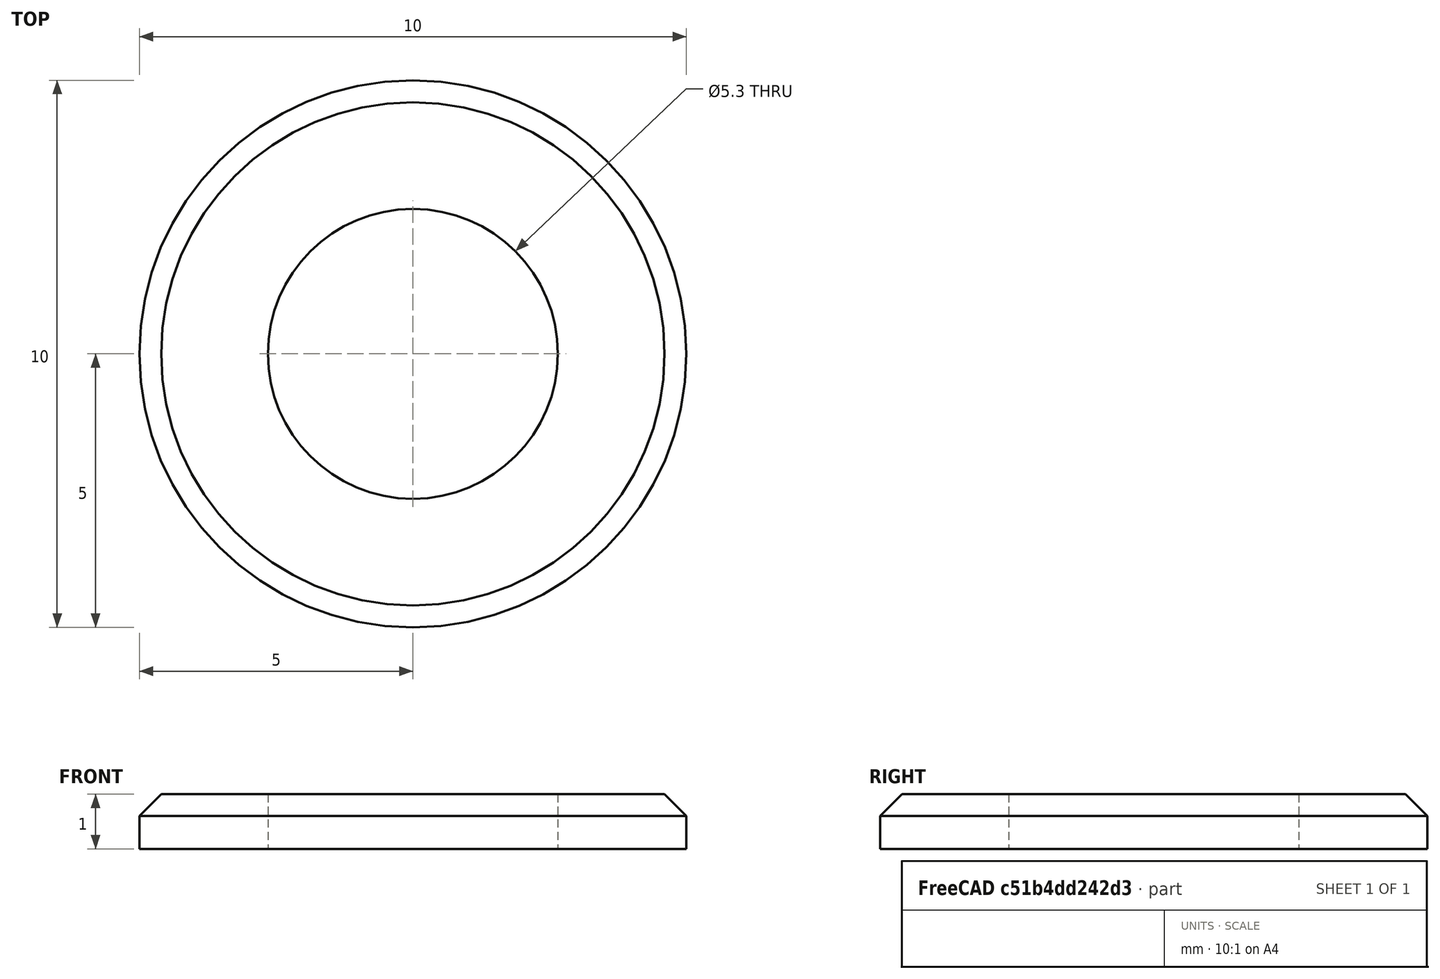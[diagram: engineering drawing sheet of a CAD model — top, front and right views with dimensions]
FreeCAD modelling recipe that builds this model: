
FCSTD DOCUMENT  (FreeCAD 0.15R4651 (Git))
Label: Scheibe_DIN125-B 5,3
License: CC-BY 3.0
LicenseURL: http://creativecommons.org/licenses/by/3.0/
objects: Sketcher::SketchObject×1, PartDesign::Revolution×1
note: 3 computed .brp shape members not serialized (recipe doc carries the construction recipe); baked Part::Feature solids carry a one-line shape summary decoded from their .brp

FEATURE [Sketcher::SketchObject] Sketch
  Placement = pos=(0,0,0) rot=(0.57735,0.57735,0.57735;2.0944rad)
  sketch-geometry (5):
    g0: LineSegment StartX=2.65 StartY=0 StartZ=0 EndX=5 EndY=0 EndZ=0
    g1: LineSegment StartX=5 StartY=0 StartZ=0 EndX=5 EndY=0.6 EndZ=0
    g2: LineSegment StartX=4.6 StartY=1 StartZ=0 EndX=2.65 EndY=1 EndZ=0
    g3: LineSegment StartX=2.65 StartY=1 StartZ=0 EndX=2.65 EndY=0 EndZ=0
    g4: LineSegment StartX=4.6 StartY=1 StartZ=0 EndX=5 EndY=0.6 EndZ=0
  constraints (15):
    c: Coincident(g0,g1)
    c: Coincident(g2,g3)
    c: Coincident(g3,g0)
    c: Horizontal(g0)
    c: Horizontal(g2)
    c: Vertical(g1)
    c: Vertical(g3)
    c: PointOnObject(g0,g-1)
    c: DistanceX(g-1,g2) = 2.65
    c: Coincident(g1,g4)
    c: Coincident(g2,g4)
    c: DistanceY(g3) = -1
    c: DistanceX(g-1,g1) = 5
    c: DistanceX(g4) = 0.4
    c: DistanceY(g4) = -0.4
FEATURE [PartDesign::Revolution] Revolution  label="Scheibe DIN 125 - B 5,3 #"
  Angle = 360
  Axis = (0,0,1)
  Base = (0,0,0)
  Placement = pos=(0,0,0) rot=(0.57735,0.57735,0.57735;2.0944rad)
  ReferenceAxis = -> Sketch [V_Axis]
  Reversed = true
  Sketch = -> Sketch
